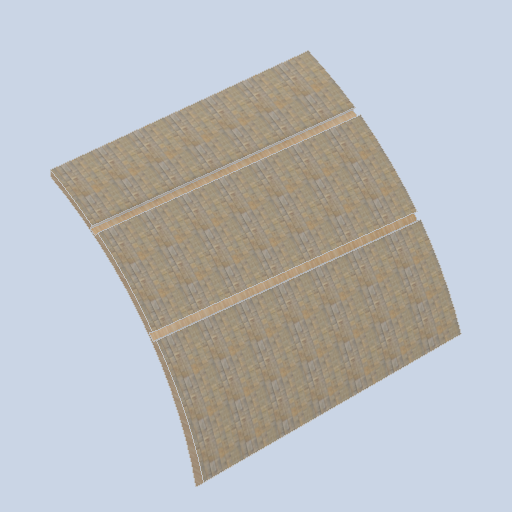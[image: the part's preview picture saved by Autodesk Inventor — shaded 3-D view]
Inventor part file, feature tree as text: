
AUTODESK INVENTOR PART (.ipt)
format: ipt  version: 2024.2 (Build 282272000, 272)  size: 344,064 bytes
history: native  units: in
note: dims shown in document units (in); Inventor stores cm internally (conversion verified against a paired STEP export)
features: other x3, sketch x2, plane x2
ambient origin geometry x8: Origin, YZ Plane, XZ Plane, XY Plane, X Axis, Y Axis, Z Axis, Center Point
bodies: Solid1 (feature_tree)
feature tree (7):
  other  "panel_block_02.ipt"
  other  "Solid1::panel_block_02.ipt"
  other  "TaggingFeature1"
  sketch  "Sketch1"  dims[d0=0.3937in]
  sketch  "Sketch2"
  plane  "Work Plane1"
  plane  "Work Plane2"
